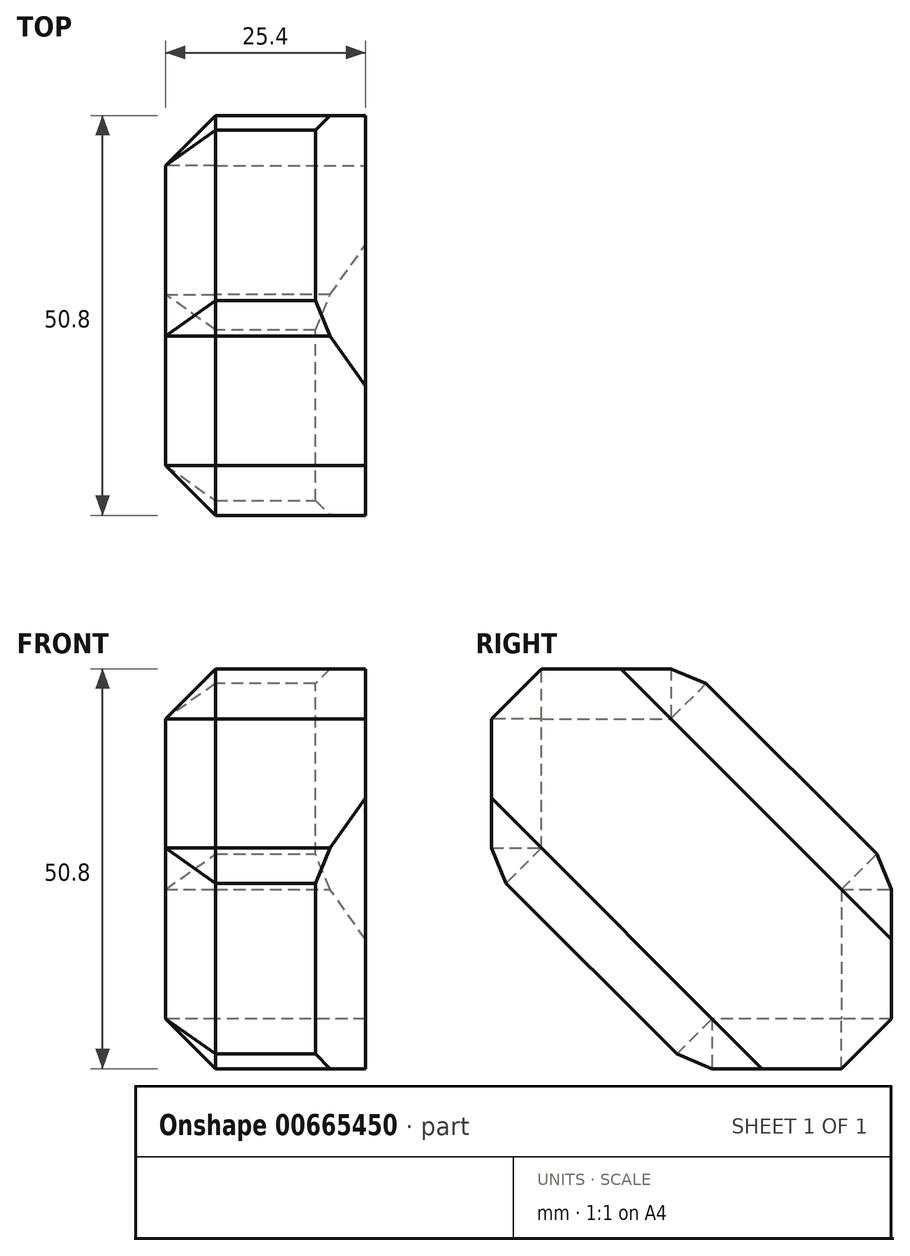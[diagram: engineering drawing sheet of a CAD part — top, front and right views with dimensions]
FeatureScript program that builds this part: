
annotation { "Feature Type Name" : "Feature", "Feature Type Description" : "" }
export const myFeature = defineFeature(function(context is Context, id is Id, definition is map)
    precondition{}
    {
        {
            var Q0;
            Q0=qCreatedBy(makeId("Top.planeOp"),FACE);
            var sketch = newSketch(context, id + "F0", { "sketchPlane" : qUnion([Q0])});
            skLineSegment(sketch, "E0.bottom", {"start": v(0, 0) * mm, "end": v(50.8, 0) * mm});
            skLineSegment(sketch, "E0.top", {"start": v(0, 50.8) * mm, "end": v(50.8, 50.8) * mm});
            skLineSegment(sketch, "E0.left", {"start": v(0, 0) * mm, "end": v(0, 50.8) * mm});
            skLineSegment(sketch, "E0.right", {"start": v(50.8, 0) * mm, "end": v(50.8, 50.8) * mm});
            skSolve(sketch);
        }
        {
            var Q0;
            Q0=makeQuery(id+"F0.imprint","IMPRINT",FACE,{"disambiguationData":[TD([[makeQuery(id+"F0.imprint","IMPRINT",EDGE,{"derivedFrom":sQuery(id+"F0.wireOp",EDGE,"E0.bottom")}),1.0]])]});
            extrude(context, id + "F1", {"entities" : qUnion([Q0]), "depth" : 50.8 * mm, "offsetDistance" : 25.4 * mm});
        }
        {
            var Q0;
            Q0=makeQuery(id+"F1.opExtrude","SWEPT_FACE",FACE,{"disambiguationData":[OSD([sQuery(id+"F0.wireOp",EDGE,"E0.right")])]});
            extrude(context, id + "F2", {"entities" : qUnion([Q0]), "operationType" : NewBodyOperationType.REMOVE, "oppositeDirection" : true, "depth" : 25.4 * mm, "offsetDistance" : 25.4 * mm});
        }
        {
            var Q0;
            Q0=makeQuery(id+"F1.opExtrude","CAP_EDGE",EDGE,{"disambiguationData":[OSD([sQuery(id+"F0.wireOp",EDGE,"E0.top")])],"isStart":false});
            chamfer(context, id + "F3", {"entities" : qUnion([Q0]), "width" : 25.4 * mm, "tangentPropagation" : true});
        }
        {
            var Q0;
            Q0=makeQuery(id+"F1.opExtrude","CAP_EDGE",EDGE,{"disambiguationData":[OSD([sQuery(id+"F0.wireOp",EDGE,"E0.bottom")])],"isStart":true});
            chamfer(context, id + "F4", {"entities" : qUnion([Q0]), "width" : 25.4 * mm, "tangentPropagation" : true});
        }
        {
            var Q0;
            Q0=makeQuery(id+"F1.opExtrude","CAP_EDGE",EDGE,{"disambiguationData":[OSD([sQuery(id+"F0.wireOp",EDGE,"E0.left")])],"isStart":false});
            var Q1;
            {var subQ0=sQuery(id+"F0.wireOp",EDGE,"E0.right");Q1=makeQuery(id+"F2.boolean.opBoolean","COPY",EDGE,{"derivedFrom":makeQuery(id+"F2.opExtrude","CAP_EDGE",EDGE,{"disambiguationData":[OSD([subQ0]),TDD([makeQuery(id+"F1.opExtrude","CAP_EDGE",EDGE,{"disambiguationData":[OSD([subQ0])],"isStart":false})])],"isStart":false})});}
            var Q2;
            Q2=makeQuery(id+"F2.boolean.opBoolean","COPY",EDGE,{"derivedFrom":makeQuery(id+"F2.opExtrude","CAP_EDGE",EDGE,{"disambiguationData":[OSD([sQuery(id+"F0.wireOp",EDGE,"E0.bottom"),sQuery(id+"F0.wireOp",EDGE,"E0.right")])],"isStart":false})});
            var Q3;
            Q3=makeQuery(id+"F1.opExtrude","SWEPT_EDGE",EDGE,{"disambiguationData":[OSD([sQuery(id+"F0.wireOp",EDGE,"E0.bottom"),sQuery(id+"F0.wireOp",EDGE,"E0.left")])]});
            var Q4;
            Q4=makeQuery(id+"F4.opChamfer","BLEND_EDGE",EDGE,{"blendedFrom":[makeQuery(id+"F1.opExtrude","CAP_EDGE",EDGE,{"disambiguationData":[OSD([sQuery(id+"F0.wireOp",EDGE,"E0.bottom")])],"isStart":true}),makeQuery(id+"F1.opExtrude","SWEPT_FACE",FACE,{"disambiguationData":[OSD([sQuery(id+"F0.wireOp",EDGE,"E0.left")])]})],"blendedInto":[makeQuery(id+"F1.opExtrude","SWEPT_FACE",FACE,{"disambiguationData":[OSD([sQuery(id+"F0.wireOp",EDGE,"E0.left")])]})]});
            var Q5;
            Q5=makeQuery(id+"F4.opChamfer","BLEND_EDGE",EDGE,{"blendedFrom":[makeQuery(id+"F1.opExtrude","CAP_EDGE",EDGE,{"disambiguationData":[OSD([sQuery(id+"F0.wireOp",EDGE,"E0.bottom")])],"isStart":true}),makeQuery(id+"F2.boolean.opBoolean","COPY",FACE,{"derivedFrom":makeQuery(id+"F2.opExtrude","CAP_FACE",FACE,{"disambiguationData":[OSD([sQuery(id+"F0.wireOp",EDGE,"E0.right")])],"isStart":false})})],"blendedInto":[makeQuery(id+"F2.boolean.opBoolean","COPY",FACE,{"derivedFrom":makeQuery(id+"F2.opExtrude","CAP_FACE",FACE,{"disambiguationData":[OSD([sQuery(id+"F0.wireOp",EDGE,"E0.right")])],"isStart":false})})]});
            var Q6;
            Q6=makeQuery(id+"F1.opExtrude","CAP_EDGE",EDGE,{"disambiguationData":[OSD([sQuery(id+"F0.wireOp",EDGE,"E0.left")])],"isStart":true});
            var Q7;
            {var subQ0=sQuery(id+"F0.wireOp",EDGE,"E0.right");Q7=makeQuery(id+"F2.boolean.opBoolean","COPY",EDGE,{"derivedFrom":makeQuery(id+"F2.opExtrude","CAP_EDGE",EDGE,{"disambiguationData":[OSD([subQ0]),TDD([makeQuery(id+"F1.opExtrude","CAP_EDGE",EDGE,{"disambiguationData":[OSD([subQ0])],"isStart":true})])],"isStart":false})});}
            var Q8;
            Q8=makeQuery(id+"F2.boolean.opBoolean","COPY",EDGE,{"derivedFrom":makeQuery(id+"F2.opExtrude","CAP_EDGE",EDGE,{"disambiguationData":[OSD([sQuery(id+"F0.wireOp",EDGE,"E0.top"),sQuery(id+"F0.wireOp",EDGE,"E0.right")])],"isStart":false})});
            var Q9;
            Q9=makeQuery(id+"F1.opExtrude","SWEPT_EDGE",EDGE,{"disambiguationData":[OSD([sQuery(id+"F0.wireOp",EDGE,"E0.top"),sQuery(id+"F0.wireOp",EDGE,"E0.left")])]});
            var Q10;
            Q10=makeQuery(id+"F3.opChamfer","BLEND_EDGE",EDGE,{"blendedFrom":[makeQuery(id+"F1.opExtrude","CAP_EDGE",EDGE,{"disambiguationData":[OSD([sQuery(id+"F0.wireOp",EDGE,"E0.top")])],"isStart":false}),makeQuery(id+"F1.opExtrude","SWEPT_FACE",FACE,{"disambiguationData":[OSD([sQuery(id+"F0.wireOp",EDGE,"E0.left")])]})],"blendedInto":[makeQuery(id+"F1.opExtrude","SWEPT_FACE",FACE,{"disambiguationData":[OSD([sQuery(id+"F0.wireOp",EDGE,"E0.left")])]})]});
            var Q11;
            Q11=makeQuery(id+"F3.opChamfer","BLEND_EDGE",EDGE,{"blendedFrom":[makeQuery(id+"F1.opExtrude","CAP_EDGE",EDGE,{"disambiguationData":[OSD([sQuery(id+"F0.wireOp",EDGE,"E0.top")])],"isStart":false}),makeQuery(id+"F2.boolean.opBoolean","COPY",FACE,{"derivedFrom":makeQuery(id+"F2.opExtrude","CAP_FACE",FACE,{"disambiguationData":[OSD([sQuery(id+"F0.wireOp",EDGE,"E0.right")])],"isStart":false})})],"blendedInto":[makeQuery(id+"F2.boolean.opBoolean","COPY",FACE,{"derivedFrom":makeQuery(id+"F2.opExtrude","CAP_FACE",FACE,{"disambiguationData":[OSD([sQuery(id+"F0.wireOp",EDGE,"E0.right")])],"isStart":false})})]});
            var Q12;
            {var subQ0=sQuery(id+"F0.wireOp",EDGE,"E0.top");Q12=makeQuery(id+"F3.opChamfer","BLEND_EDGE",EDGE,{"blendedFrom":[makeQuery(id+"F1.opExtrude","CAP_EDGE",EDGE,{"disambiguationData":[OSD([subQ0])],"isStart":false}),makeQuery(id+"F1.opExtrude","SWEPT_FACE",FACE,{"disambiguationData":[OSD([subQ0])]})],"blendedInto":[makeQuery(id+"F1.opExtrude","SWEPT_FACE",FACE,{"disambiguationData":[OSD([subQ0])]})]});}
            var Q13;
            {var subQ0=sQuery(id+"F0.wireOp",EDGE,"E0.top");Q13=makeQuery(id+"F3.opChamfer","BLEND_EDGE",EDGE,{"blendedFrom":[makeQuery(id+"F1.opExtrude","CAP_EDGE",EDGE,{"disambiguationData":[OSD([subQ0])],"isStart":false}),makeQuery(id+"F1.opExtrude","CAP_FACE",FACE,{"disambiguationData":[OSD([sQuery(id+"F0.wireOp",EDGE,"E0.bottom"),subQ0,sQuery(id+"F0.wireOp",EDGE,"E0.left"),sQuery(id+"F0.wireOp",EDGE,"E0.right")])],"isStart":false})],"blendedInto":[makeQuery(id+"F1.opExtrude","CAP_FACE",FACE,{"disambiguationData":[OSD([sQuery(id+"F0.wireOp",EDGE,"E0.bottom"),subQ0,sQuery(id+"F0.wireOp",EDGE,"E0.left"),sQuery(id+"F0.wireOp",EDGE,"E0.right")])],"isStart":false})]});}
            var Q14;
            {var subQ0=sQuery(id+"F0.wireOp",EDGE,"E0.bottom");Q14=makeQuery(id+"F4.opChamfer","BLEND_EDGE",EDGE,{"blendedFrom":[makeQuery(id+"F1.opExtrude","CAP_EDGE",EDGE,{"disambiguationData":[OSD([subQ0])],"isStart":true}),makeQuery(id+"F1.opExtrude","SWEPT_FACE",FACE,{"disambiguationData":[OSD([subQ0])]})],"blendedInto":[makeQuery(id+"F1.opExtrude","SWEPT_FACE",FACE,{"disambiguationData":[OSD([subQ0])]})]});}
            var Q15;
            {var subQ0=sQuery(id+"F0.wireOp",EDGE,"E0.bottom");Q15=makeQuery(id+"F4.opChamfer","BLEND_EDGE",EDGE,{"blendedFrom":[makeQuery(id+"F1.opExtrude","CAP_EDGE",EDGE,{"disambiguationData":[OSD([subQ0])],"isStart":true}),makeQuery(id+"F1.opExtrude","CAP_FACE",FACE,{"disambiguationData":[OSD([subQ0,sQuery(id+"F0.wireOp",EDGE,"E0.top"),sQuery(id+"F0.wireOp",EDGE,"E0.left"),sQuery(id+"F0.wireOp",EDGE,"E0.right")])],"isStart":true})],"blendedInto":[makeQuery(id+"F1.opExtrude","CAP_FACE",FACE,{"disambiguationData":[OSD([subQ0,sQuery(id+"F0.wireOp",EDGE,"E0.top"),sQuery(id+"F0.wireOp",EDGE,"E0.left"),sQuery(id+"F0.wireOp",EDGE,"E0.right")])],"isStart":true})]});}
            var Q16;
            Q16=makeQuery(id+"F1.opExtrude","CAP_EDGE",EDGE,{"disambiguationData":[OSD([sQuery(id+"F0.wireOp",EDGE,"E0.top")])],"isStart":true});
            var Q17;
            Q17=makeQuery(id+"F1.opExtrude","CAP_EDGE",EDGE,{"disambiguationData":[OSD([sQuery(id+"F0.wireOp",EDGE,"E0.bottom")])],"isStart":false});
            chamfer(context, id + "F5", {"entities" : qUnion([Q0, Q1, Q2, Q3, Q4, Q5, Q6, Q7, Q8, Q9, Q10, Q11, Q12, Q13, Q14, Q15, Q16, Q17]), "width" : 6.35 * mm, "tangentPropagation" : true});
        }
    });
